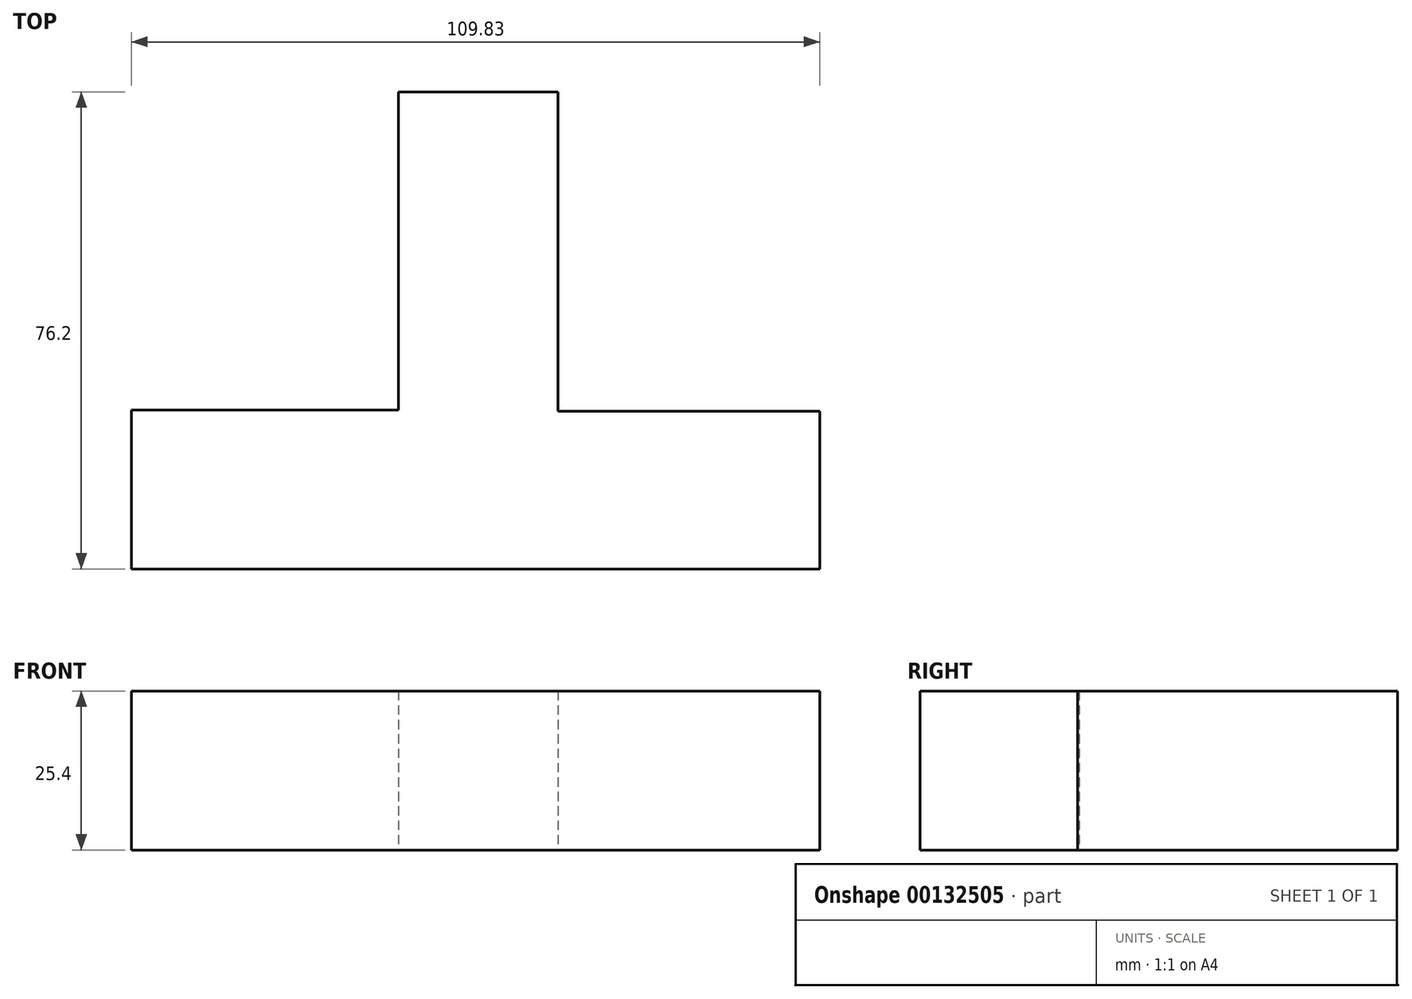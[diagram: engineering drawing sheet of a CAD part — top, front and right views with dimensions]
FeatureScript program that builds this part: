
annotation { "Feature Type Name" : "Feature", "Feature Type Description" : "" }
export const myFeature = defineFeature(function(context is Context, id is Id, definition is map)
    precondition{}
    {
        {
            var Q0;
            Q0=qCreatedBy(makeId("Top.planeOp"),FACE);
            var sketch = newSketch(context, id + "F0", { "sketchPlane" : qUnion([Q0])});
            skLineSegment(sketch, "E0", {"start": v(0, 0) * mm, "end": v(57.02, 0) * mm});
            skLineSegment(sketch, "E1", {"start": v(57.02, 0) * mm, "end": v(57.02, 25.19) * mm});
            skLineSegment(sketch, "E2", {"start": v(57.02, 25.19) * mm, "end": v(15.26, 25.19) * mm});
            skLineSegment(sketch, "E3", {"start": v(15.26, 25.19) * mm, "end": v(15.26, 76.2) * mm});
            skLineSegment(sketch, "E4", {"start": v(15.26, 76.2) * mm, "end": v(-10.24, 76.2) * mm});
            skLineSegment(sketch, "E5", {"start": v(-10.24, 76.2) * mm, "end": v(-10.24, 25.4) * mm});
            skLineSegment(sketch, "E6", {"start": v(-10.24, 25.4) * mm, "end": v(-52.8, 25.4) * mm});
            skLineSegment(sketch, "E7", {"start": v(-52.8, 25.4) * mm, "end": v(-52.8, 0) * mm});
            skLineSegment(sketch, "E8", {"start": v(-52.8, 0) * mm, "end": v(0, 0) * mm});
            skSolve(sketch);
        }
        {
            var Q0;
            Q0 = qSketchRegion(id + "F0", true);
            extrude(context, id + "F1", {"entities" : qUnion([Q0]), "depth" : 25.4 * mm});
        }
    });
